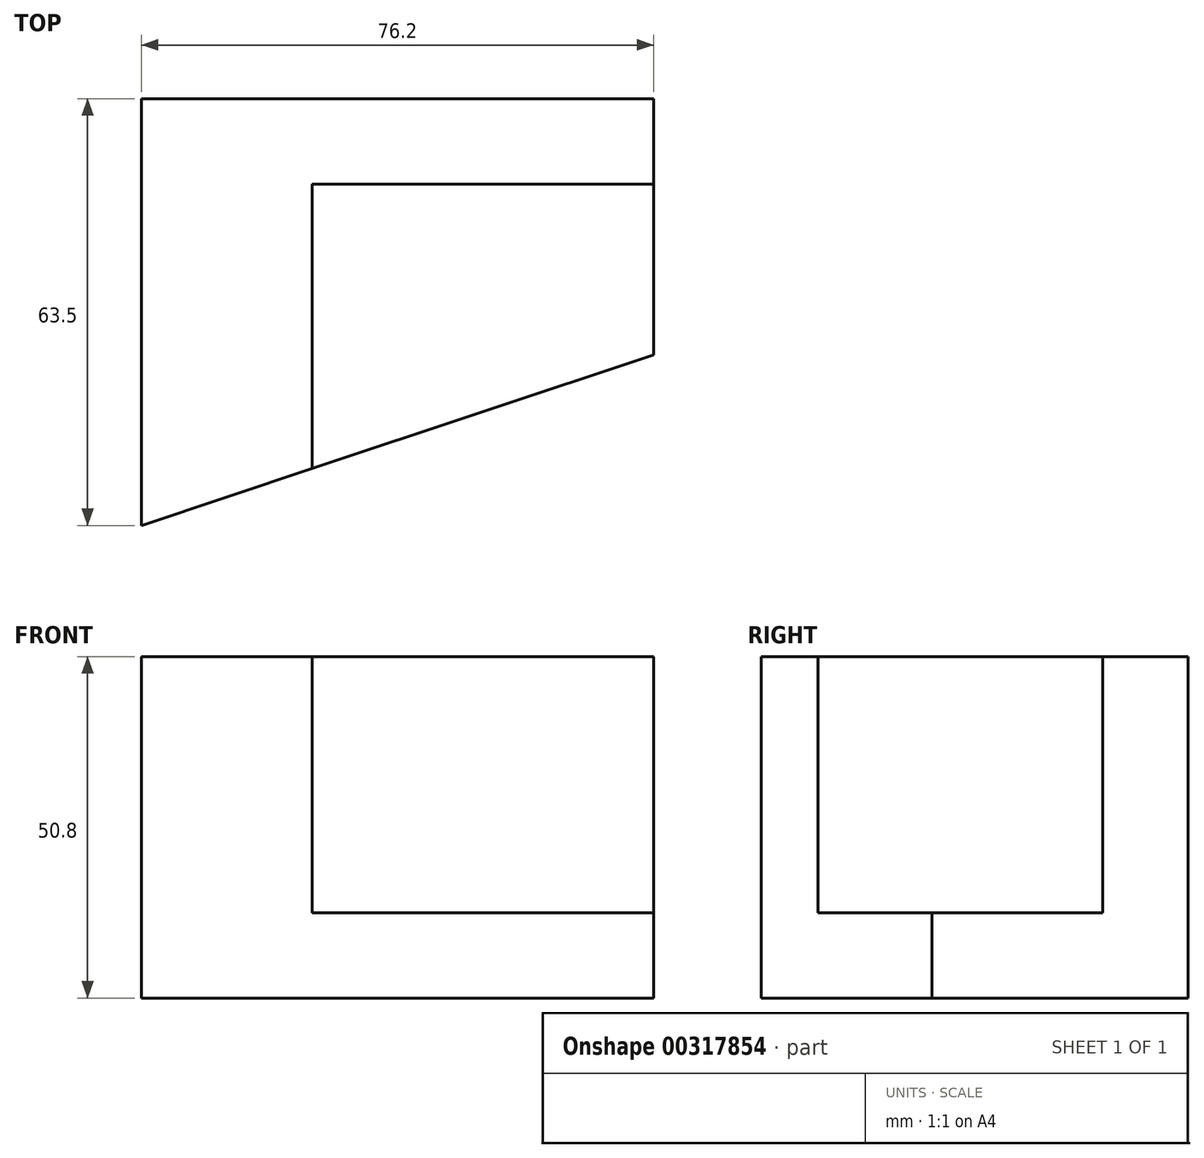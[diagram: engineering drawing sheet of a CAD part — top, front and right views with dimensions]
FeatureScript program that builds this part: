
annotation { "Feature Type Name" : "Feature", "Feature Type Description" : "" }
export const myFeature = defineFeature(function(context is Context, id is Id, definition is map)
    precondition{}
    {
        {
            var Q0;
            Q0=qCreatedBy(makeId("Front.planeOp"),FACE);
            var sketch = newSketch(context, id + "F0", { "sketchPlane" : qUnion([Q0])});
            skLineSegment(sketch, "E0.bottom", {"start": v(0, 0) * mm, "end": v(76.2, 0) * mm});
            skLineSegment(sketch, "E0.top", {"start": v(0, 50.8) * mm, "end": v(76.2, 50.8) * mm});
            skLineSegment(sketch, "E0.left", {"start": v(0, 0) * mm, "end": v(0, 50.8) * mm});
            skLineSegment(sketch, "E0.right", {"start": v(76.2, 0) * mm, "end": v(76.2, 50.8) * mm});
            skSolve(sketch);
        }
        {
            var Q0;
            Q0 = qSketchRegion(id + "F0", true);
            extrude(context, id + "F1", {"entities" : qUnion([Q0]), "depth" : 63.5 * mm});
        }
        {
            var Q0;
            Q0=makeQuery(id+"F1.opExtrude","SWEPT_FACE",FACE,{"disambiguationData":[OSD([sQuery(id+"F0.wireOp",EDGE,"E0.top")])]});
            var sketch = newSketch(context, id + "F2", { "sketchPlane" : qUnion([Q0])});
            skLineSegment(sketch, "E1.bottom", {"start": v(25.4, -63.5) * mm, "end": v(76.2, -63.5) * mm});
            skLineSegment(sketch, "E1.top", {"start": v(25.4, -12.7) * mm, "end": v(76.2, -12.7) * mm});
            skLineSegment(sketch, "E1.left", {"start": v(25.4, -63.5) * mm, "end": v(25.4, -12.7) * mm});
            skLineSegment(sketch, "E1.right", {"start": v(76.2, -63.5) * mm, "end": v(76.2, -12.7) * mm});
            skSolve(sketch);
        }
        {
            var Q0;
            Q0 = qSketchRegion(id + "F2", true);
            extrude(context, id + "F3", {"entities" : qUnion([Q0]), "operationType" : NewBodyOperationType.REMOVE, "oppositeDirection" : true, "depth" : 38.1 * mm});
        }
        {
            var Q0;
            Q0=makeQuery(id+"F1.opExtrude","SWEPT_FACE",FACE,{"disambiguationData":[OSD([sQuery(id+"F0.wireOp",EDGE,"E0.top")])]});
            var sketch = newSketch(context, id + "F4", { "sketchPlane" : qUnion([Q0])});
            skLineSegment(sketch, "E2", {"start": v(76.2, -63.5) * mm, "end": v(76.2, -38.1) * mm});
            skLineSegment(sketch, "E3", {"start": v(76.2, -38.1) * mm, "end": v(0, -63.5) * mm});
            skLineSegment(sketch, "E4", {"start": v(0, -63.5) * mm, "end": v(76.2, -63.5) * mm});
            skSolve(sketch);
        }
        {
            var Q0;
            Q0 = qSketchRegion(id + "F4", true);
            extrude(context, id + "F5", {"entities" : qUnion([Q0]), "operationType" : NewBodyOperationType.REMOVE, "endBound" : BoundingType.THROUGH_ALL, "oppositeDirection" : true, "depth" : 25.4 * mm});
        }
    });
